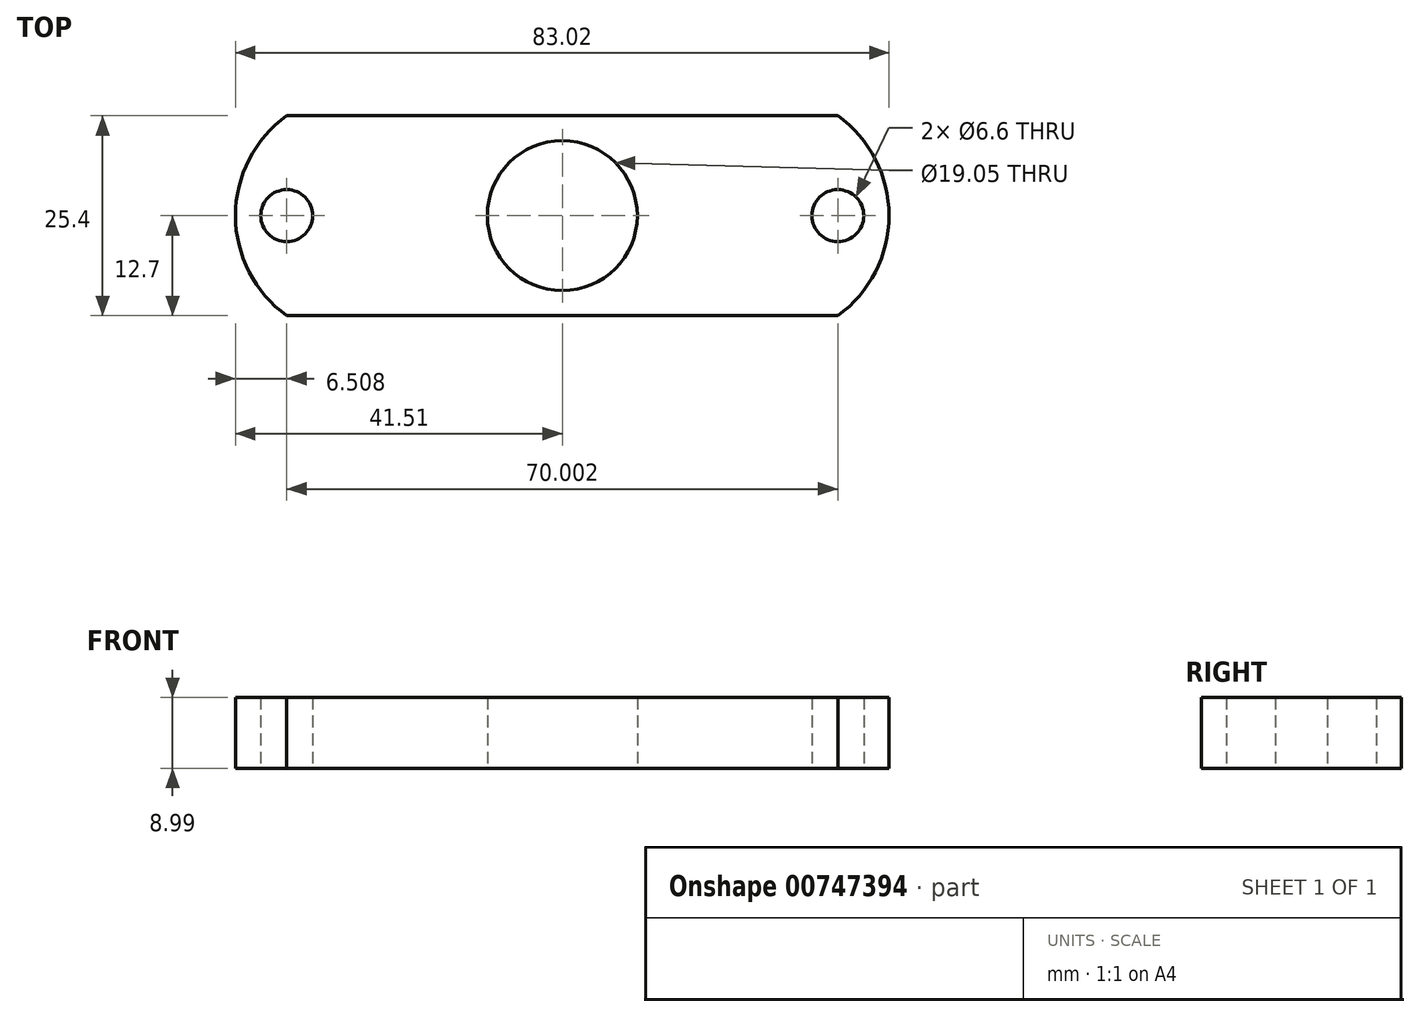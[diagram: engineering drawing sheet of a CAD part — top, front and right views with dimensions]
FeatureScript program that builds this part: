
annotation { "Feature Type Name" : "Feature", "Feature Type Description" : "" }
export const myFeature = defineFeature(function(context is Context, id is Id, definition is map)
    precondition{}
    {
        {
            var Q0;
            Q0=qCreatedBy(makeId("Top.planeOp"),FACE);
            var sketch = newSketch(context, id + "F0", { "sketchPlane" : qUnion([Q0])});
            skLineSegment(sketch, "E0.bottom", {"start": v(9.45, 0) * mm, "end": v(79.45, 0) * mm});
            skLineSegment(sketch, "E0.top", {"start": v(9.45, -25.4) * mm, "end": v(79.45, -25.4) * mm});
            skPoint(sketch, "E1", {"position": v(44.45, 0) * mm});
            skPoint(sketch, "E2", {"position": v(0, -12.7) * mm});
            skCircle(sketch, "E3", {"center": v(44.45, -12.7) * mm, "radius": 9.53 * mm});
            skPoint(sketch, "E4", {"position": v(9.45, -12.7) * mm});
            skPoint(sketch, "E5", {"position": v(79.45, -12.7) * mm});
            skCircle(sketch, "E6", {"center": v(9.45, -12.7) * mm, "radius": 3.3 * mm});
            skCircle(sketch, "E7", {"center": v(79.45, -12.7) * mm, "radius": 3.3 * mm});
            skArc(sketch, "E8", {"start": v(9.45, 0) * mm, "mid": v(2.94, -12.7) * mm, "end": v(9.45, -25.4) * mm});
            skArc(sketch, "E9", {"start": v(79.45, -25.4) * mm, "mid": v(85.96, -12.7) * mm, "end": v(79.45, 0) * mm});
            skPoint(sketch, "E10.orphan", {"position": v(0, 0) * mm});
            skPoint(sketch, "E11.orphan", {"position": v(0, -25.4) * mm});
            skPoint(sketch, "E12.orphan", {"position": v(88.9, 0) * mm});
            skPoint(sketch, "E13.end.orphan", {"position": v(9.45, -19.05) * mm});
            skPoint(sketch, "E13.start.orphan", {"position": v(9.45, -6.35) * mm});
            skSolve(sketch);
        }
        {
            var Q0;
            Q0=makeQuery(id+"F0.imprint","IMPRINT",FACE,{"disambiguationData":[TD([[makeQuery(id+"F0.imprint","IMPRINT",EDGE,{"derivedFrom":sQuery(id+"F0.wireOp",EDGE,"E0.bottom")}),-1.0]])]});
            extrude(context, id + "F1", {"entities" : qUnion([Q0]), "depth" : 9 * mm, "offsetDistance" : 25.4 * mm});
        }
    });
